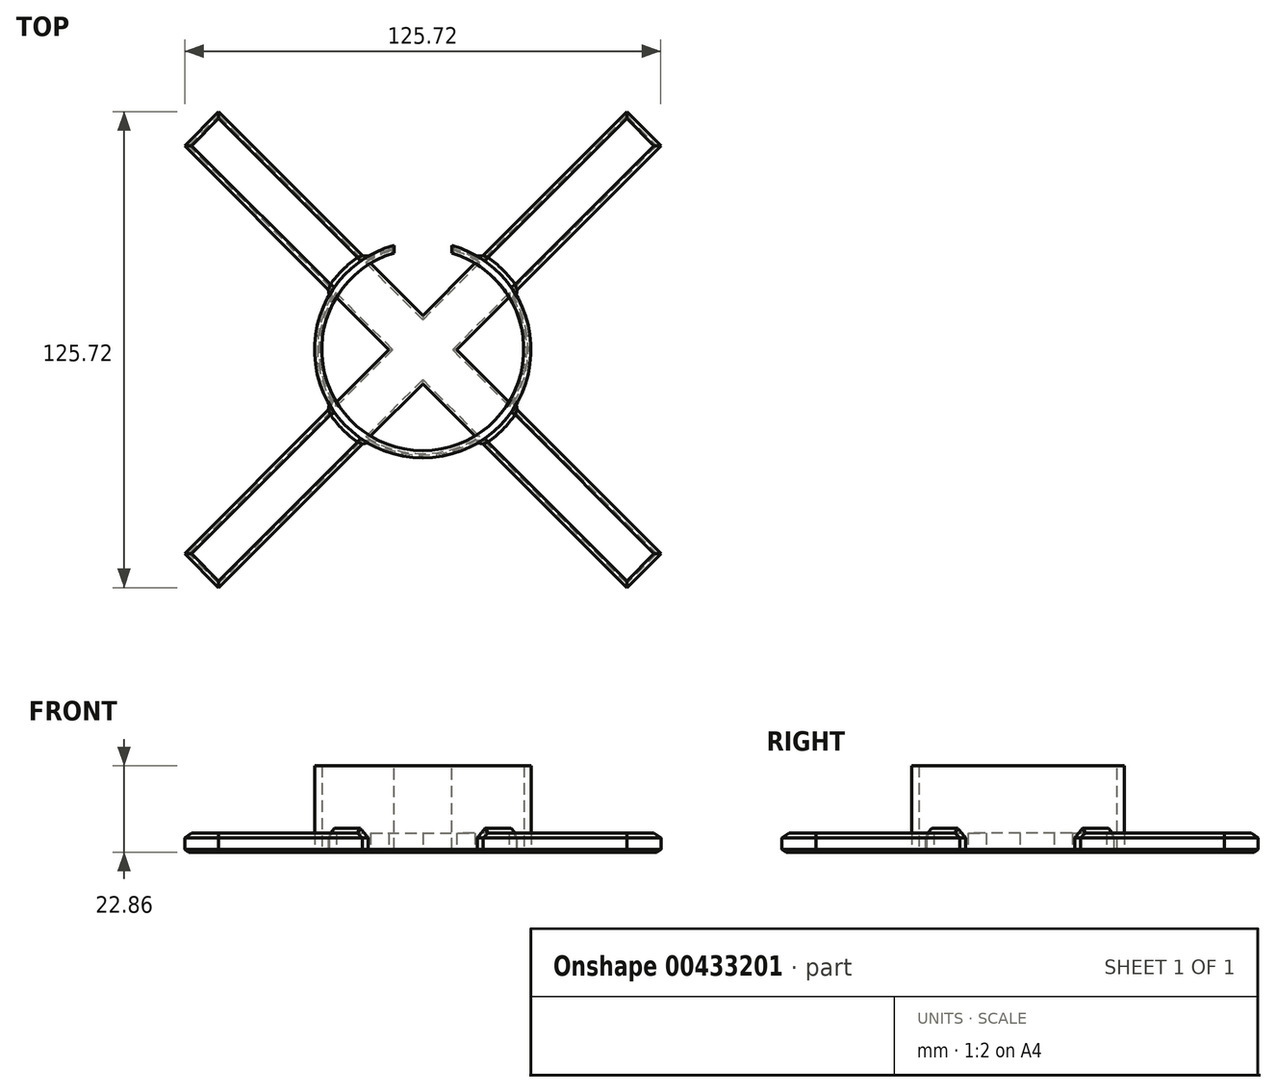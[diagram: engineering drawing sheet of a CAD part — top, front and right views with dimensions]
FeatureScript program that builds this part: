
annotation { "Feature Type Name" : "Feature", "Feature Type Description" : "" }
export const myFeature = defineFeature(function(context is Context, id is Id, definition is map)
    precondition{}
    {
        {
            var Q0;
            Q0=qCreatedBy(makeId("Top.planeOp"),FACE);
            var sketch = newSketch(context, id + "F0", { "sketchPlane" : qUnion([Q0])});
            skCircle(sketch, "E0", {"center": v(0, 0) * mm, "radius": 28.57 * mm});
            skCircle(sketch, "E1", {"center": v(0, 0) * mm, "radius": 26.67 * mm});
            skSolve(sketch);
        }
        {
            var Q0;
            Q0 = qSketchRegion(id + "F0", true);
            extrude(context, id + "F1", {"entities" : qUnion([Q0]), "depth" : 22.86 * mm, "offsetDistance" : 25.4 * mm});
        }
        {
            var Q0;
            Q0=makeQuery(id+"F1.opExtrude","CAP_FACE",FACE,{"disambiguationData":[OSD([sQuery(id+"F0.wireOp",EDGE,"E0"),sQuery(id+"F0.wireOp",EDGE,"E1")])],"isStart":true});
            var sketch = newSketch(context, id + "F2", { "sketchPlane" : qUnion([Q0])});
            skLineSegment(sketch, "E2", {"start": v(0, 8.98) * mm, "end": v(53.88, 62.86) * mm});
            skLineSegment(sketch, "E3", {"start": v(53.88, 62.86) * mm, "end": v(62.86, 53.88) * mm});
            skLineSegment(sketch, "E4", {"start": v(62.86, 53.88) * mm, "end": v(8.98, 0) * mm});
            skLineSegment(sketch, "E5", {"start": v(8.98, 0) * mm, "end": v(62.86, -53.88) * mm});
            skLineSegment(sketch, "E6", {"start": v(62.86, -53.88) * mm, "end": v(53.88, -62.86) * mm});
            skLineSegment(sketch, "E7", {"start": v(53.88, -62.86) * mm, "end": v(0, -8.98) * mm});
            skLineSegment(sketch, "E8", {"start": v(0, -8.98) * mm, "end": v(-53.88, -62.86) * mm});
            skLineSegment(sketch, "E9", {"start": v(-53.88, -62.86) * mm, "end": v(-62.86, -53.88) * mm});
            skLineSegment(sketch, "E10", {"start": v(-62.86, -53.88) * mm, "end": v(-8.98, 0) * mm});
            skLineSegment(sketch, "E11", {"start": v(-8.98, 0) * mm, "end": v(-62.86, 53.88) * mm});
            skLineSegment(sketch, "E12", {"start": v(-62.86, 53.88) * mm, "end": v(-53.88, 62.86) * mm});
            skLineSegment(sketch, "E13", {"start": v(-53.88, 62.86) * mm, "end": v(0, 8.98) * mm});
            skSolve(sketch);
        }
        {
            var Q0;
            Q0 = qSketchRegion(id + "F2", true);
            extrude(context, id + "F3", {"entities" : qUnion([Q0]), "operationType" : NewBodyOperationType.ADD, "oppositeDirection" : true, "depth" : 5.08 * mm, "offsetDistance" : 25.4 * mm});
        }
        {
            var Q0;
            {var subQ0=sQuery(id+"F2.wireOp",EDGE,"E2");var subQ1=sQuery(id+"F2.wireOp",EDGE,"E3");var subQ2=sQuery(id+"F2.wireOp",EDGE,"E4");Q0=makeQuery(id+"F3.boolean.opBoolean","SPLIT",FACE,{"disambiguationData":[TD([makeQuery(id+"F3.opExtrude","SWEPT_FACE",FACE,{"disambiguationData":[OSD([subQ1])]})])],"derivedFrom":makeQuery(id+"F3.opExtrude","CAP_FACE",FACE,{"disambiguationData":[OSD([subQ0,subQ1,subQ2,sQuery(id+"F2.wireOp",EDGE,"E5"),sQuery(id+"F2.wireOp",EDGE,"E6"),sQuery(id+"F2.wireOp",EDGE,"E7"),sQuery(id+"F2.wireOp",EDGE,"E8"),sQuery(id+"F2.wireOp",EDGE,"E9"),sQuery(id+"F2.wireOp",EDGE,"E10"),sQuery(id+"F2.wireOp",EDGE,"E11"),sQuery(id+"F2.wireOp",EDGE,"E12"),sQuery(id+"F2.wireOp",EDGE,"E13")])],"isStart":false})});}
            var Q1;
            {var subQ0=sQuery(id+"F2.wireOp",EDGE,"E12");var subQ1=sQuery(id+"F2.wireOp",EDGE,"E11");var subQ2=sQuery(id+"F2.wireOp",EDGE,"E13");Q1=makeQuery(id+"F3.boolean.opBoolean","SPLIT",FACE,{"disambiguationData":[TD([makeQuery(id+"F3.opExtrude","SWEPT_FACE",FACE,{"disambiguationData":[OSD([subQ0])]})])],"derivedFrom":makeQuery(id+"F3.opExtrude","CAP_FACE",FACE,{"disambiguationData":[OSD([sQuery(id+"F2.wireOp",EDGE,"E2"),sQuery(id+"F2.wireOp",EDGE,"E3"),sQuery(id+"F2.wireOp",EDGE,"E4"),sQuery(id+"F2.wireOp",EDGE,"E5"),sQuery(id+"F2.wireOp",EDGE,"E6"),sQuery(id+"F2.wireOp",EDGE,"E7"),sQuery(id+"F2.wireOp",EDGE,"E8"),sQuery(id+"F2.wireOp",EDGE,"E9"),sQuery(id+"F2.wireOp",EDGE,"E10"),subQ1,subQ0,subQ2])],"isStart":false})});}
            var Q2;
            {var subQ0=sQuery(id+"F2.wireOp",EDGE,"E8");var subQ1=sQuery(id+"F2.wireOp",EDGE,"E9");var subQ2=sQuery(id+"F2.wireOp",EDGE,"E10");Q2=makeQuery(id+"F3.boolean.opBoolean","SPLIT",FACE,{"disambiguationData":[TD([makeQuery(id+"F3.opExtrude","SWEPT_FACE",FACE,{"disambiguationData":[OSD([subQ1])]})])],"derivedFrom":makeQuery(id+"F3.opExtrude","CAP_FACE",FACE,{"disambiguationData":[OSD([sQuery(id+"F2.wireOp",EDGE,"E2"),sQuery(id+"F2.wireOp",EDGE,"E3"),sQuery(id+"F2.wireOp",EDGE,"E4"),sQuery(id+"F2.wireOp",EDGE,"E5"),sQuery(id+"F2.wireOp",EDGE,"E6"),sQuery(id+"F2.wireOp",EDGE,"E7"),subQ0,subQ1,subQ2,sQuery(id+"F2.wireOp",EDGE,"E11"),sQuery(id+"F2.wireOp",EDGE,"E12"),sQuery(id+"F2.wireOp",EDGE,"E13")])],"isStart":false})});}
            var Q3;
            {var subQ0=sQuery(id+"F2.wireOp",EDGE,"E7");var subQ1=sQuery(id+"F2.wireOp",EDGE,"E5");var subQ2=sQuery(id+"F2.wireOp",EDGE,"E6");Q3=makeQuery(id+"F3.boolean.opBoolean","SPLIT",FACE,{"disambiguationData":[TD([makeQuery(id+"F3.opExtrude","SWEPT_FACE",FACE,{"disambiguationData":[OSD([subQ2])]})])],"derivedFrom":makeQuery(id+"F3.opExtrude","CAP_FACE",FACE,{"disambiguationData":[OSD([sQuery(id+"F2.wireOp",EDGE,"E2"),sQuery(id+"F2.wireOp",EDGE,"E3"),sQuery(id+"F2.wireOp",EDGE,"E4"),subQ1,subQ2,subQ0,sQuery(id+"F2.wireOp",EDGE,"E8"),sQuery(id+"F2.wireOp",EDGE,"E9"),sQuery(id+"F2.wireOp",EDGE,"E10"),sQuery(id+"F2.wireOp",EDGE,"E11"),sQuery(id+"F2.wireOp",EDGE,"E12"),sQuery(id+"F2.wireOp",EDGE,"E13")])],"isStart":false})});}
            chamfer(context, id + "F4", {"entities" : qUnion([Q0, Q1, Q2, Q3]), "width" : 1.27 * mm, "tangentPropagation" : true});
        }
        {
            var Q0;
            Q0=makeQuery(id+"F1.opExtrude","CAP_FACE",FACE,{"disambiguationData":[OSD([sQuery(id+"F0.wireOp",EDGE,"E0"),sQuery(id+"F0.wireOp",EDGE,"E1")])],"isStart":false});
            var sketch = newSketch(context, id + "F5", { "sketchPlane" : qUnion([Q0])});
            skLineSegment(sketch, "E14.bottom", {"start": v(-7.62, 28.57) * mm, "end": v(7.62, 28.57) * mm});
            skLineSegment(sketch, "E14.top", {"start": v(-7.62, 25.56) * mm, "end": v(7.62, 25.56) * mm});
            skLineSegment(sketch, "E14.left", {"start": v(-7.62, 28.57) * mm, "end": v(-7.62, 25.56) * mm});
            skLineSegment(sketch, "E14.right", {"start": v(7.62, 28.57) * mm, "end": v(7.62, 25.56) * mm});
            skSolve(sketch);
        }
        {
            var Q0;
            Q0 = qSketchRegion(id + "F5", true);
            extrude(context, id + "F6", {"entities" : qUnion([Q0]), "operationType" : NewBodyOperationType.REMOVE, "oppositeDirection" : true, "depth" : 25.4 * mm, "offsetDistance" : 25.4 * mm});
        }
        {
            var Q0;
            Q0=makeQuery(id+"F3.boolean.opBoolean","MERGE",FACE,{"derivedFrom":[makeQuery(id+"F1.opExtrude","CAP_FACE",FACE,{"disambiguationData":[OSD([sQuery(id+"F0.wireOp",EDGE,"E0"),sQuery(id+"F0.wireOp",EDGE,"E1")])],"isStart":true}),makeQuery(id+"F3.opExtrude","CAP_FACE",FACE,{"disambiguationData":[OSD([sQuery(id+"F2.wireOp",EDGE,"E2"),sQuery(id+"F2.wireOp",EDGE,"E3"),sQuery(id+"F2.wireOp",EDGE,"E4"),sQuery(id+"F2.wireOp",EDGE,"E5"),sQuery(id+"F2.wireOp",EDGE,"E6"),sQuery(id+"F2.wireOp",EDGE,"E7"),sQuery(id+"F2.wireOp",EDGE,"E8"),sQuery(id+"F2.wireOp",EDGE,"E9"),sQuery(id+"F2.wireOp",EDGE,"E10"),sQuery(id+"F2.wireOp",EDGE,"E11"),sQuery(id+"F2.wireOp",EDGE,"E12"),sQuery(id+"F2.wireOp",EDGE,"E13")])],"isStart":true})]});
            chamfer(context, id + "F7", {"entities" : qUnion([Q0]), "width" : 0.76 * mm, "tangentPropagation" : true});
        }
    });
